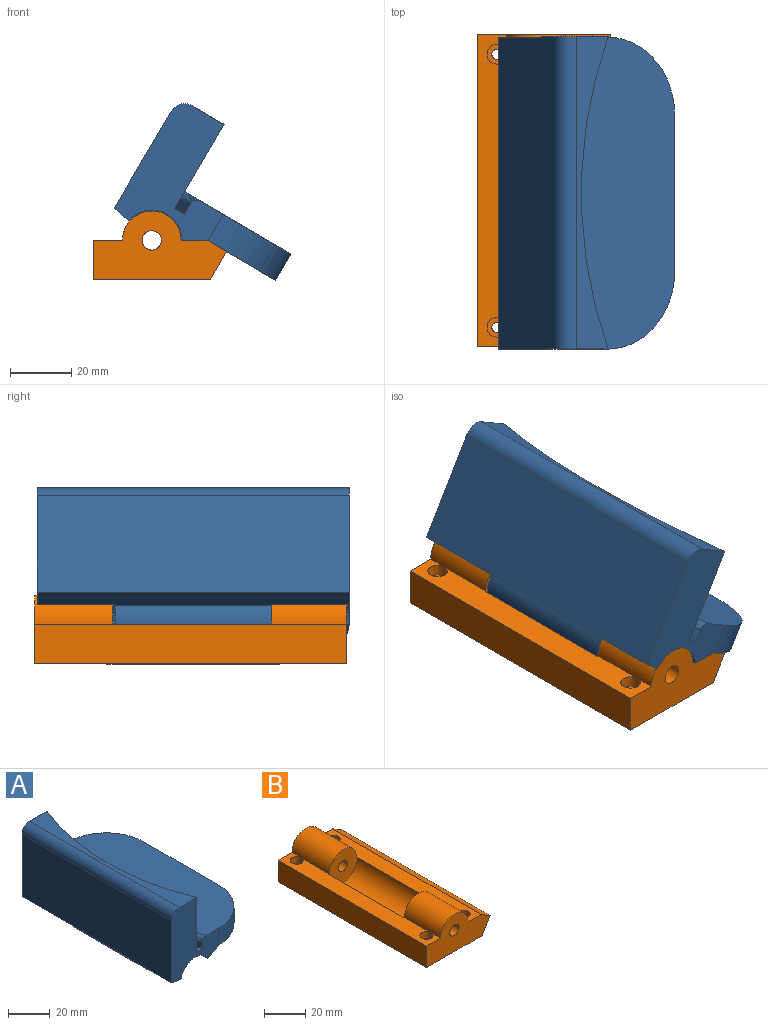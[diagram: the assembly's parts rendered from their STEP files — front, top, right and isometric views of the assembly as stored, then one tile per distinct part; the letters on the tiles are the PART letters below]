
ASSEMBLY  parts=2 mates=1
PART A: 22 faces, bbox 57.6x112.2x54 mm
  f0: cylinder r=3.17mm len=50.8mm, axis (0,-1,0), area 1013.4mm2, adj f13,f15
  f1: cylinder r=9.53mm len=50.8mm, axis (0,-1,0), area 1857.9mm2, adj f10,f11,f13,f15
  f2: plane 42.73x31.75mm, normal (0,-1,0), area 793mm2, adj f4,f5,f6,f7,f8,f9,f10,f11
  f3: plane 42.73x31.75mm, normal (0,1,0), area 793mm2, adj f4,f5,f6,f7,f8,f9,f10,f11
  f4: plane 101.6x44.32mm, normal (0,0,1), area 3874.9mm2, adj f2,f3,f9,f19,f20,f21
  f5: plane 101.6x36.57mm, normal (-1,0,0), area 3715.6mm2, adj f2,f3,f11,f17
  f6: cylinder r=133.35mm len=101.6mm, axis (0,0,1), area 3309.4mm2, adj f2,f3,f8,f16
  f7: cylinder r=130.05mm len=101.6mm, axis (0,0,1), area 397.7mm2, adj f2,f3,f8,f9
  f8: plane 101.6x13.63mm, normal (0,0,1), area 344.4mm2, adj f2,f3,f6,f7
  f9: torus R=127.51mm, axis (0,0,1), area 416.6mm2, adj f2,f3,f4,f7
  f10: plane 101.6x7.63mm, normal (0.5,0,-0.87), area 875.3mm2, adj f1,f2,f3,f12,f13,f14,f15,f18
  f11: plane 101.6x6.49mm, normal (-0.17,0,-0.98), area 650.7mm2, adj f1,f2,f3,f5,f12,f13,f14,f15
  f12: cylinder r=9.91mm len=25.4mm, axis (0,-1,0), area 614.8mm2, adj f2,f10,f11,f13
  f13: plane 19.43x19.28mm, normal (0,-1,0), area 262.4mm2, adj f0,f1,f10,f11,f12
  f14: cylinder r=9.91mm len=25.4mm, axis (0,1,0), area 614.8mm2, adj f3,f10,f11,f15
  f15: plane 19.43x19.28mm, normal (0,1,0), area 262.4mm2, adj f0,f1,f10,f11,f14
  f16: plane 101.6x11.96mm, normal (0,0,1), area 528.8mm2, adj f2,f3,f6,f17
  f17: cylinder r=5.08mm len=101.6mm, axis (0,1,0), area 810.7mm2, adj f2,f3,f5,f16
  f18: plane 101.6x25.4mm, normal (0,0,-1), area 2303.7mm2, adj f10,f19,f20,f21
  f19: plane 50.8x9.88mm, normal (1,0,0), area 502.1mm2, adj f4,f18,f20,f21
  f20: cylinder r=25.4mm len=25.4mm, axis (0,0,-1), area 394.4mm2, adj f3,f4,f18,f19
  f21: cylinder r=25.4mm len=25.4mm, axis (0,0,1), area 394.4mm2, adj f2,f4,f18,f19
PART B: 27 faces, bbox 43.4x101.6x22.2 mm
  f0: cylinder r=1.59mm len=8.89mm, axis (0,0,1), area 88.7mm2, adj f6,f24
  f1: cylinder r=1.59mm len=8.89mm, axis (0,0,1), area 88.7mm2, adj f6,f22
  f2: cylinder r=1.59mm len=8.89mm, axis (0,0,1), area 88.7mm2, adj f6,f20
  f3: cylinder r=1.59mm len=8.89mm, axis (0,0,1), area 88.7mm2, adj f6,f18
  f4: plane 101.6x9.53mm, normal (0,0,1), area 884.8mm2, adj f8,f10,f11,f12,f13,f14,f15,f16
  f5: plane 101.6x8.81mm, normal (0,0,1), area 812.5mm2, adj f8,f10,f11,f12,f14,f15,f16,f21
  f6: plane 101.6x38.1mm, normal (0,0,-1), area 3839.3mm2, adj f0,f1,f2,f3,f11,f12,f13,f26
  f7: cylinder r=3.17mm len=25.4mm, axis (0,-1,0), area 506.7mm2, adj f11,f15
  f8: cylinder r=9.53mm len=25.4mm, axis (0,-1,0), area 760.1mm2, adj f4,f5,f11,f15
  f9: cylinder r=3.17mm len=24.64mm, axis (0,-1,0), area 491.5mm2, adj f12,f16
  f10: cylinder r=9.53mm len=24.64mm, axis (0,-1,0), area 737.3mm2, adj f4,f5,f12,f16
  f11: plane 43.42x22.23mm, normal (0,1,0), area 627.3mm2, adj f4,f5,f6,f7,f8,f13,f25,f26
  f12: plane 43.42x22.23mm, normal (0,-1,0), area 627.3mm2, adj f4,f5,f6,f9,f10,f13,f25,f26
  f13: plane 101.6x12.7mm, normal (-1,0,0), area 1290.3mm2, adj f4,f6,f11,f12
  f14: cylinder r=9.91mm len=51.56mm, axis (0,-1,0), area 1604.6mm2, adj f4,f5,f15,f16
  f15: plane 19.81x19.43mm, normal (0,-1,0), area 265mm2, adj f4,f5,f7,f8,f14
  f16: plane 19.81x19.43mm, normal (0,1,0), area 265mm2, adj f4,f5,f9,f10,f14
  f17: cylinder r=3.17mm len=6.35mm, axis (0,0,1), area 76mm2, adj f4,f18
  f18: plane 6.35x6.35mm, normal (0,0,1), area 23.8mm2, adj f3,f17
  f19: cylinder r=3.17mm len=6.35mm, axis (0,0,1), area 76mm2, adj f4,f20
  f20: plane 6.35x6.35mm, normal (0,0,1), area 23.8mm2, adj f2,f19
  f21: cylinder r=3.17mm len=6.35mm, axis (0,0,1), area 76mm2, adj f5,f22
  f22: plane 6.35x6.35mm, normal (0,0,1), area 23.8mm2, adj f1,f21
  f23: cylinder r=3.17mm len=6.35mm, axis (0,0,1), area 76mm2, adj f5,f24
  f24: plane 6.35x6.35mm, normal (0,0,1), area 23.8mm2, adj f0,f23
  f25: plane 101.6x6.03mm, normal (0.5,0,0.87), area 707.7mm2, adj f5,f11,f12,f26
  f26: plane 101.6x9.22mm, normal (0.87,0,-0.5), area 1081.3mm2, adj f6,f11,f12,f25
PLACE A rot(axis=(0,1,0),30.4deg) t=(98,4.96,-44.83)mm
PLACE B t=(-9.3,5.72,5.53)mm fixed
MATE revolute A.f1 <-> B.f7  axis (0,-1,0) through (-9.3,-20.44,18.23)mm
